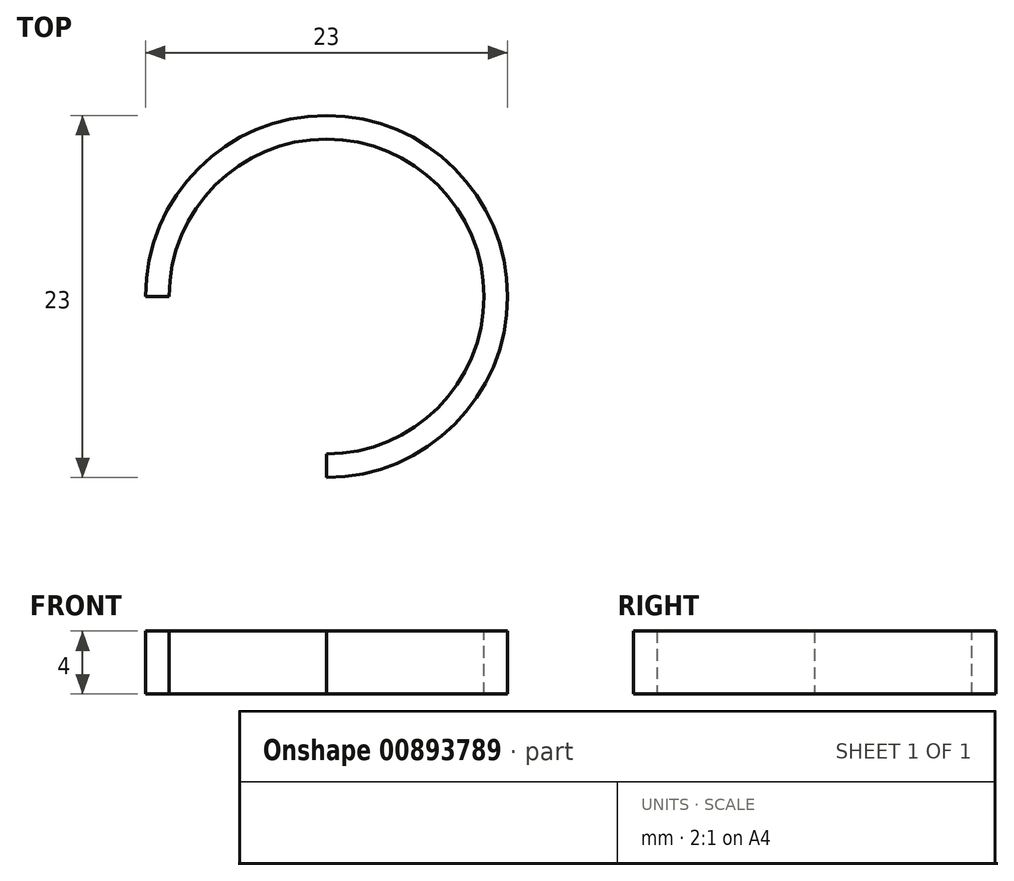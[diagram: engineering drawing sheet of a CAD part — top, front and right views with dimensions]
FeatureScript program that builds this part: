
annotation { "Feature Type Name" : "Feature", "Feature Type Description" : "" }
export const myFeature = defineFeature(function(context is Context, id is Id, definition is map)
    precondition{}
    {
        {
            var Q0;
            Q0=qCreatedBy(makeId("Front.planeOp"),FACE);
            var sketch = newSketch(context, id + "F0", { "sketchPlane" : qUnion([Q0])});
            skLineSegment(sketch, "E0.bottom", {"start": v(-11.5, -18.48) * mm, "end": v(-10, -18.48) * mm});
            skLineSegment(sketch, "E0.top", {"start": v(-11.5, -22.48) * mm, "end": v(-10, -22.48) * mm});
            skLineSegment(sketch, "E0.left", {"start": v(-11.5, -18.48) * mm, "end": v(-11.5, -22.48) * mm});
            skLineSegment(sketch, "E0.right", {"start": v(-10, -18.48) * mm, "end": v(-10, -22.48) * mm});
            skSolve(sketch);
        }
        {
            var Q0;
            Q0=qCreatedBy(makeId("Front.planeOp"),FACE);
            var sketch = newSketch(context, id + "F1", { "sketchPlane" : qUnion([Q0])});
            skLineSegment(sketch, "E1", {"start": v(0, -8.33) * mm, "end": v(0, -32.06) * mm, "construction": true});
            skSolve(sketch);
        }
        {
            var Q0;
            Q0=makeQuery(id+"F0.imprint","IMPRINT",FACE,{"disambiguationData":[TD([[makeQuery(id+"F0.imprint","IMPRINT",EDGE,{"derivedFrom":sQuery(id+"F0.wireOp",EDGE,"E0.bottom")}),-1.0]])]});
            var Q1;
            Q1=sQuery(id+"F1.wireOp",EDGE,"E1");
            revolve(context, id + "F2", {"surfaceOperationType" : NewSurfaceOperationType.NEW, "entities" : qUnion([Q0]), "axis" : qUnion([Q1]), "revolveType" : RevolveType.ONE_DIRECTION, "angle" : 270 * degree});
        }
    });
